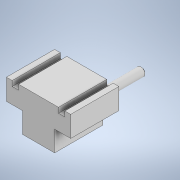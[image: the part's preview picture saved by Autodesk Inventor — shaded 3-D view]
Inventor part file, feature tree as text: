
AUTODESK INVENTOR PART (.ipt)
format: ipt  version: 2020 (Build 240168000, 168)  size: 152,064 bytes
history: native  units: in
note: dims shown in document units (in); Inventor stores cm internally (conversion verified against a paired STEP export)
features: extrude x4, sketch x4, chamfer x2, plane x1
ambient origin geometry x8: Origin, YZ Plane, XZ Plane, XY Plane, X Axis, Y Axis, Z Axis, Center Point
bodies: Solid1 (feature_tree)
feature tree (11):
  plane  "Work Plane1"
  extrude  "Extrusion1"  Depth=3.937in
  extrude  "Extrusion2"  Depth=2.5591in
  extrude  "Extrusion3"  Depth=5.9055in TaperAngle=0.0deg
  chamfer  "Chamfer1"  Distance=6.6929in
  chamfer  "Chamfer2"  Distance=1.5748in
  extrude  "Extrusion4"  Depth=1.5748in
  sketch  "Sketch1"  dims[d0=7.874in d1=3.937in]
  sketch  "Sketch2"  dims[d2=7.4016in d3=2.5591in]
  sketch  "Sketch3"  dims[d5=1.9685in d6=5.9055in d7=0.0in]
  sketch  "Sketch4"  dims[d8=1.0236in d9=6.6929in d10=0.0in d11=1.5748in d12=1.5748in d13=2.3622in d14=0.0in d15=0.1969in d16=0.0787in d17=45.0deg d18=0.0787in d19=0.0787in d20=45.0deg d21=2.5197in d22=0.7874in d23=0.6299in d24=0.7087in d25=0.0in d26=0.0in]
